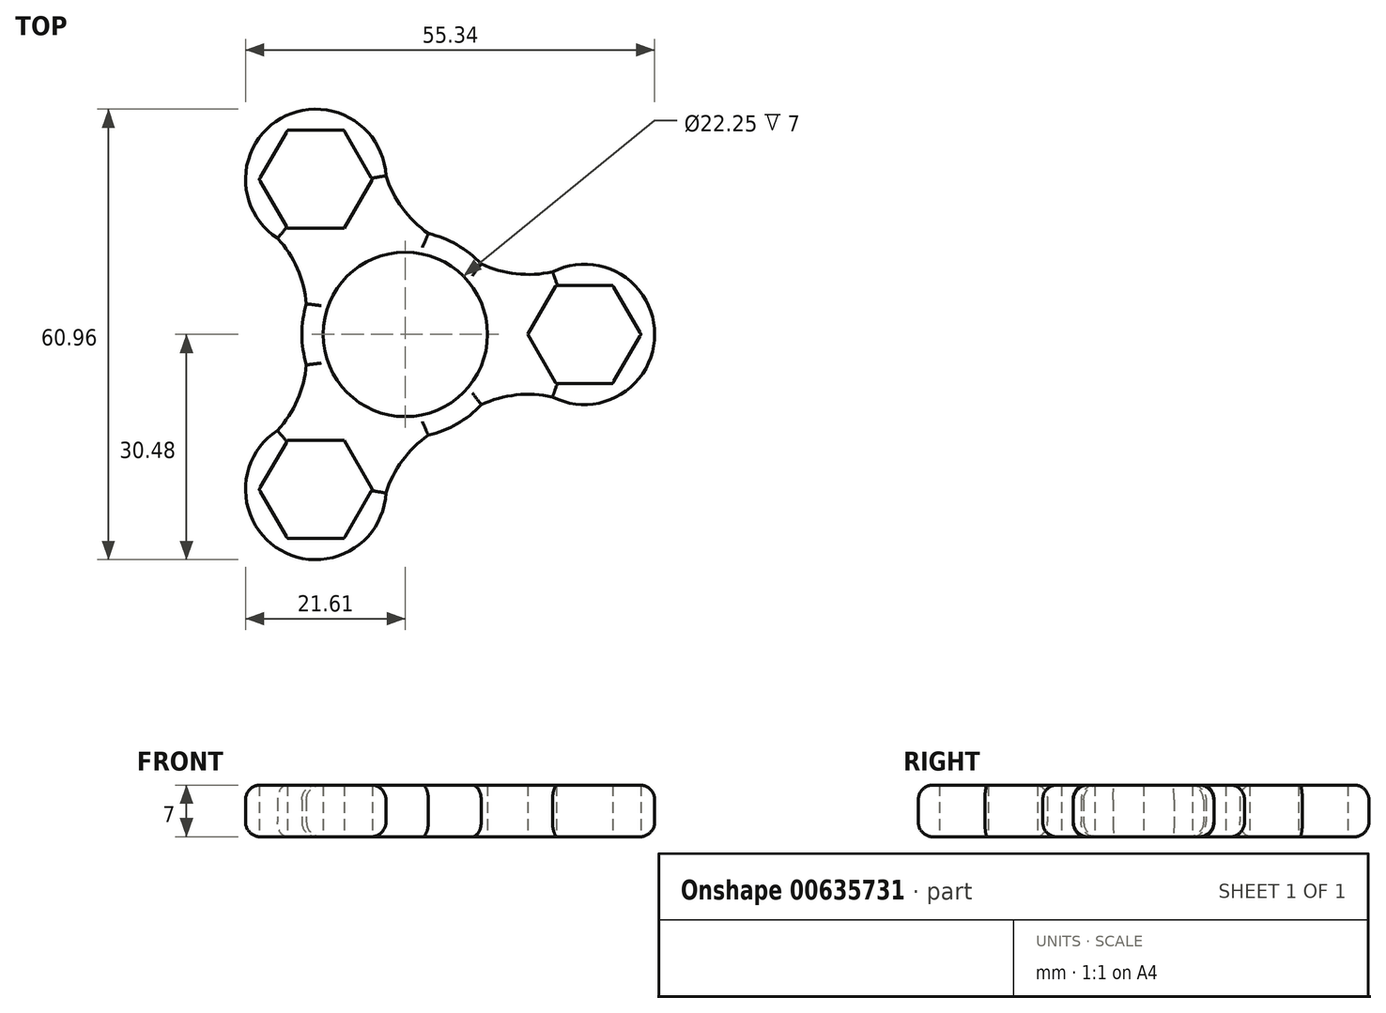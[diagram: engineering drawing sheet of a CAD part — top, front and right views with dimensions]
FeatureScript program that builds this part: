
annotation { "Feature Type Name" : "Feature", "Feature Type Description" : "" }
export const myFeature = defineFeature(function(context is Context, id is Id, definition is map)
    precondition{}
    {
        {
            var Q0;
            Q0=qCreatedBy(makeId("Top.planeOp"),FACE);
            var sketch = newSketch(context, id + "F0", { "sketchPlane" : qUnion([Q0])});
            skCircle(sketch, "E0", {"center": v(0, 0) * mm, "radius": 11.12 * mm});
            skLineSegment(sketch, "E1", {"start": v(0, 0) * mm, "end": v(30, 0) * mm, "construction": true});
            skCircle(sketch, "E2", {"center": v(24.23, 0) * mm, "radius": 9.5 * mm});
            skCircle(sketch, "E3", {"center": v(0, 0) * mm, "radius": 14 * mm});
            skArc(sketch, "E4", {"start": v(19.9, -8.46) * mm, "mid": v(15, -8.2) * mm, "end": v(10.26, -9.52) * mm});
            skArc(sketch, "E5.MirrorCS", {"start": v(19.9, 8.46) * mm, "mid": v(15, 8.2) * mm, "end": v(10.26, 9.52) * mm});
            skCircle(sketch, "E6.cCircle", {"center": v(24.23, 0) * mm, "radius": 6.62 * mm, "construction": true});
            skLineSegment(sketch, "E6.0", {"start": v(20.4, 6.62) * mm, "end": v(28.05, 6.62) * mm});
            skLineSegment(sketch, "E6.1", {"start": v(28.05, 6.62) * mm, "end": v(31.88, 0) * mm});
            skLineSegment(sketch, "E6.2", {"start": v(31.88, 0) * mm, "end": v(28.05, -6.62) * mm});
            skLineSegment(sketch, "E6.3", {"start": v(28.05, -6.62) * mm, "end": v(20.4, -6.63) * mm});
            skLineSegment(sketch, "E6.4", {"start": v(20.4, -6.63) * mm, "end": v(16.58, 0) * mm});
            skLineSegment(sketch, "E6.5", {"start": v(16.58, 0) * mm, "end": v(20.4, 6.63) * mm});
            skPoint(sketch, "E6.0.midPoint", {"position": v(24.23, 6.62) * mm});
            skLineSegment(sketch, "E7.1.0", {"start": v(-15.94, 14.36) * mm, "end": v(-19.76, 20.98) * mm});
            skArc(sketch, "E7.1.1", {"start": v(-2.63, 21.47) * mm, "mid": v(-0.4, 17.09) * mm, "end": v(3.12, 13.65) * mm});
            skLineSegment(sketch, "E7.1.2", {"start": v(-15.94, 27.6) * mm, "end": v(-8.29, 27.6) * mm});
            skArc(sketch, "E7.1.3", {"start": v(-17.28, 13.01) * mm, "mid": v(-14.6, 8.9) * mm, "end": v(-13.38, 4.12) * mm});
            skCircle(sketch, "E7.1.4", {"center": v(-12.11, 20.98) * mm, "radius": 6.62 * mm, "construction": true});
            skLineSegment(sketch, "E7.1.5", {"start": v(0, 0) * mm, "end": v(-15, 25.98) * mm, "construction": true});
            skCircle(sketch, "E7.1.6", {"center": v(-12.11, 20.98) * mm, "radius": 9.5 * mm});
            skLineSegment(sketch, "E7.1.7", {"start": v(-19.76, 20.98) * mm, "end": v(-15.94, 27.6) * mm});
            skLineSegment(sketch, "E7.1.8", {"start": v(-8.29, 27.6) * mm, "end": v(-4.46, 20.98) * mm});
            skLineSegment(sketch, "E7.1.9", {"start": v(-4.46, 20.98) * mm, "end": v(-8.29, 14.36) * mm});
            skLineSegment(sketch, "E7.1.10", {"start": v(-8.29, 14.36) * mm, "end": v(-15.94, 14.36) * mm});
            skPoint(sketch, "E7.1.11", {"position": v(-17.85, 17.67) * mm});
            skLineSegment(sketch, "E7.2.0", {"start": v(-4.46, -20.98) * mm, "end": v(-8.29, -27.6) * mm});
            skArc(sketch, "E7.2.1", {"start": v(-17.28, -13.01) * mm, "mid": v(-14.6, -8.9) * mm, "end": v(-13.38, -4.12) * mm});
            skLineSegment(sketch, "E7.2.2", {"start": v(-15.94, -27.6) * mm, "end": v(-19.76, -20.98) * mm});
            skArc(sketch, "E7.2.3", {"start": v(-2.63, -21.47) * mm, "mid": v(-0.4, -17.09) * mm, "end": v(3.12, -13.65) * mm});
            skCircle(sketch, "E7.2.4", {"center": v(-12.11, -20.98) * mm, "radius": 6.62 * mm, "construction": true});
            skLineSegment(sketch, "E7.2.5", {"start": v(0, 0) * mm, "end": v(-15, -25.98) * mm, "construction": true});
            skCircle(sketch, "E7.2.6", {"center": v(-12.11, -20.98) * mm, "radius": 9.5 * mm});
            skLineSegment(sketch, "E7.2.7", {"start": v(-8.29, -27.6) * mm, "end": v(-15.94, -27.6) * mm});
            skLineSegment(sketch, "E7.2.8", {"start": v(-19.76, -20.98) * mm, "end": v(-15.94, -14.36) * mm});
            skLineSegment(sketch, "E7.2.9", {"start": v(-15.94, -14.36) * mm, "end": v(-8.29, -14.36) * mm});
            skLineSegment(sketch, "E7.2.10", {"start": v(-8.29, -14.36) * mm, "end": v(-4.46, -20.98) * mm});
            skPoint(sketch, "E7.2.11", {"position": v(-6.38, -24.3) * mm});
            skSolve(sketch);
        }
        {
            var Q0;
            Q0=makeQuery(id+"F0.imprint","IMPRINT",FACE,{"disambiguationData":[TD([[makeQuery(id+"F0.imprint","IMPRINT",EDGE,{"derivedFrom":sQuery(id+"F0.wireOp",EDGE,"0df89d4a-0bd4-4ad1-abb0-4ab84ff28107.1.3")}),-1.0]])]});
            var Q1;
            {var subQ0=sQuery(id+"F0.wireOp",EDGE,"0df89d4a-0bd4-4ad1-abb0-4ab84ff28107.1.0");Q1=makeQuery(id+"F0.imprint","IMPRINT",FACE,{"disambiguationData":[TD([[makeQuery(id+"F0.imprint","IMPRINT",EDGE,{"derivedFrom":subQ0}),1.0]])]});}
            var Q2;
            Q2=makeQuery(id+"F0.imprint","IMPRINT",FACE,{"disambiguationData":[TD([[makeQuery(id+"F0.imprint","IMPRINT",EDGE,{"derivedFrom":sQuery(id+"F0.wireOp",EDGE,"E0")}),-1.0]])]});
            var Q3;
            {var subQ0=sQuery(id+"F0.wireOp",EDGE,"E4");Q3=makeQuery(id+"F0.imprint","IMPRINT",FACE,{"disambiguationData":[TD([[makeQuery(id+"F0.imprint","IMPRINT",EDGE,{"derivedFrom":subQ0}),-1.0]])]});}
            var Q4;
            Q4=makeQuery(id+"F0.imprint","IMPRINT",FACE,{"disambiguationData":[TD([[makeQuery(id+"F0.imprint","IMPRINT",EDGE,{"derivedFrom":sQuery(id+"F0.wireOp",EDGE,"yqVcjg71-0tow-opGA-WTYz-QMPVO2lDSPor")}),-1.0]])]});
            var Q5;
            {var subQ0=sQuery(id+"F0.wireOp",EDGE,"0df89d4a-0bd4-4ad1-abb0-4ab84ff28107.2.0");Q5=makeQuery(id+"F0.imprint","IMPRINT",FACE,{"disambiguationData":[TD([[makeQuery(id+"F0.imprint","IMPRINT",EDGE,{"derivedFrom":subQ0}),1.0]])]});}
            var Q6;
            Q6=makeQuery(id+"F0.imprint","IMPRINT",FACE,{"disambiguationData":[TD([[makeQuery(id+"F0.imprint","IMPRINT",EDGE,{"derivedFrom":sQuery(id+"F0.wireOp",EDGE,"0df89d4a-0bd4-4ad1-abb0-4ab84ff28107.2.3")}),-1.0]])]});
            var Q7;
            Q7=makeQuery(id+"F0.imprint","IMPRINT",FACE,{"disambiguationData":[TD([[makeQuery(id+"F0.imprint","IMPRINT",EDGE,{"derivedFrom":sQuery(id+"F0.wireOp",EDGE,"d223a131-a13d-45e3-9094-9db3f5cdf163.0")}),1.0]])]});
            var Q8;
            Q8=makeQuery(id+"F0.imprint","IMPRINT",FACE,{"disambiguationData":[TD([[makeQuery(id+"F0.imprint","IMPRINT",EDGE,{"derivedFrom":sQuery(id+"F0.wireOp",EDGE,"E6.0")}),1.0]])]});
            var Q9;
            Q9=makeQuery(id+"F0.imprint","IMPRINT",FACE,{"disambiguationData":[TD([[makeQuery(id+"F0.imprint","IMPRINT",EDGE,{"derivedFrom":sQuery(id+"F0.wireOp",EDGE,"9b35a66b-6c7d-4a83-b0f2-d91667951e34.0")}),1.0]])]});
            var Q10;
            {var subQ0=sQuery(id+"F0.wireOp",EDGE,"E7.1.1");Q10=makeQuery(id+"F0.imprint","IMPRINT",FACE,{"disambiguationData":[TD([[makeQuery(id+"F0.imprint","IMPRINT",EDGE,{"derivedFrom":subQ0}),-1.0]])]});}
            var Q11;
            Q11=makeQuery(id+"F0.imprint","IMPRINT",FACE,{"disambiguationData":[TD([[makeQuery(id+"F0.imprint","IMPRINT",EDGE,{"derivedFrom":sQuery(id+"F0.wireOp",EDGE,"E7.1.0")}),1.0]])]});
            var Q12;
            {var subQ0=sQuery(id+"F0.wireOp",EDGE,"E7.2.1");Q12=makeQuery(id+"F0.imprint","IMPRINT",FACE,{"disambiguationData":[TD([[makeQuery(id+"F0.imprint","IMPRINT",EDGE,{"derivedFrom":subQ0}),-1.0]])]});}
            var Q13;
            Q13=makeQuery(id+"F0.imprint","IMPRINT",FACE,{"disambiguationData":[TD([[makeQuery(id+"F0.imprint","IMPRINT",EDGE,{"derivedFrom":sQuery(id+"F0.wireOp",EDGE,"E7.2.0")}),1.0]])]});
            extrude(context, id + "F1", {"entities" : qUnion([Q0, Q1, Q2, Q3, Q4, Q5, Q6, Q7, Q8, Q9, Q10, Q11, Q12, Q13]), "depth" : 7 * mm, "offsetDistance" : 25 * mm});
        }
        {
            var Q0;
            Q0=makeQuery(id+"F1.opExtrude","CAP_EDGE",EDGE,{"disambiguationData":[OSD([sQuery(id+"F0.wireOp",EDGE,"E7.1.6")])],"isStart":false});
            var Q1;
            Q1=makeQuery(id+"F1.opExtrude","CAP_EDGE",EDGE,{"disambiguationData":[OSD([sQuery(id+"F0.wireOp",EDGE,"E7.1.3")])],"isStart":false});
            var Q2;
            {var subQ0=sQuery(id+"F0.wireOp",EDGE,"E3");Q2=makeQuery(id+"F1.opExtrude","CAP_EDGE",EDGE,{"disambiguationData":[OSD([subQ0]),TDD([makeQuery(id+"F0.imprint","IMPRINT",EDGE,{"disambiguationData":[TD([[makeQuery(id+"F0.imprint","INTERSECT",VERTEX,{"derivedFrom":[subQ0,sQuery(id+"F0.wireOp",EDGE,"E7.1.3")]}),-1.0]])],"derivedFrom":subQ0})])],"isStart":false});}
            var Q3;
            Q3=makeQuery(id+"F1.opExtrude","CAP_EDGE",EDGE,{"disambiguationData":[OSD([sQuery(id+"F0.wireOp",EDGE,"E7.2.1")])],"isStart":false});
            var Q4;
            Q4=makeQuery(id+"F1.opExtrude","CAP_EDGE",EDGE,{"disambiguationData":[OSD([sQuery(id+"F0.wireOp",EDGE,"E7.2.6")])],"isStart":false});
            var Q5;
            Q5=makeQuery(id+"F1.opExtrude","CAP_EDGE",EDGE,{"disambiguationData":[OSD([sQuery(id+"F0.wireOp",EDGE,"E7.2.3")])],"isStart":false});
            var Q6;
            {var subQ0=sQuery(id+"F0.wireOp",EDGE,"E3");Q6=makeQuery(id+"F1.opExtrude","CAP_EDGE",EDGE,{"disambiguationData":[OSD([subQ0]),TDD([makeQuery(id+"F0.imprint","IMPRINT",EDGE,{"disambiguationData":[TD([[makeQuery(id+"F0.imprint","INTERSECT",VERTEX,{"derivedFrom":[subQ0,sQuery(id+"F0.wireOp",EDGE,"E4")]}),1.0]])],"derivedFrom":subQ0})])],"isStart":false});}
            var Q7;
            Q7=makeQuery(id+"F1.opExtrude","CAP_EDGE",EDGE,{"disambiguationData":[OSD([sQuery(id+"F0.wireOp",EDGE,"E4")])],"isStart":false});
            var Q8;
            Q8=makeQuery(id+"F1.opExtrude","CAP_EDGE",EDGE,{"disambiguationData":[OSD([sQuery(id+"F0.wireOp",EDGE,"E2")])],"isStart":false});
            var Q9;
            Q9=makeQuery(id+"F1.opExtrude","CAP_EDGE",EDGE,{"disambiguationData":[OSD([sQuery(id+"F0.wireOp",EDGE,"E5.MirrorCS")])],"isStart":false});
            var Q10;
            {var subQ0=sQuery(id+"F0.wireOp",EDGE,"E3");Q10=makeQuery(id+"F1.opExtrude","CAP_EDGE",EDGE,{"disambiguationData":[OSD([subQ0]),TDD([makeQuery(id+"F0.imprint","IMPRINT",EDGE,{"disambiguationData":[TD([[makeQuery(id+"F0.imprint","INTERSECT",VERTEX,{"derivedFrom":[subQ0,sQuery(id+"F0.wireOp",EDGE,"E5.MirrorCS")]}),-1.0]])],"derivedFrom":subQ0})])],"isStart":false});}
            var Q11;
            Q11=makeQuery(id+"F1.opExtrude","CAP_EDGE",EDGE,{"disambiguationData":[OSD([sQuery(id+"F0.wireOp",EDGE,"E7.1.1")])],"isStart":false});
            var Q12;
            Q12=makeQuery(id+"F1.opExtrude","CAP_EDGE",EDGE,{"disambiguationData":[OSD([sQuery(id+"F0.wireOp",EDGE,"E7.2.6")])],"isStart":true});
            var Q13;
            Q13=makeQuery(id+"F1.opExtrude","CAP_EDGE",EDGE,{"disambiguationData":[OSD([sQuery(id+"F0.wireOp",EDGE,"E7.2.1")])],"isStart":true});
            var Q14;
            {var subQ0=sQuery(id+"F0.wireOp",EDGE,"E3");Q14=makeQuery(id+"F1.opExtrude","CAP_EDGE",EDGE,{"disambiguationData":[OSD([subQ0]),TDD([makeQuery(id+"F0.imprint","IMPRINT",EDGE,{"disambiguationData":[TD([[makeQuery(id+"F0.imprint","INTERSECT",VERTEX,{"derivedFrom":[subQ0,sQuery(id+"F0.wireOp",EDGE,"E7.1.3")]}),-1.0]])],"derivedFrom":subQ0})])],"isStart":true});}
            var Q15;
            Q15=makeQuery(id+"F1.opExtrude","CAP_EDGE",EDGE,{"disambiguationData":[OSD([sQuery(id+"F0.wireOp",EDGE,"E7.1.3")])],"isStart":true});
            var Q16;
            Q16=makeQuery(id+"F1.opExtrude","CAP_EDGE",EDGE,{"disambiguationData":[OSD([sQuery(id+"F0.wireOp",EDGE,"E7.1.6")])],"isStart":true});
            var Q17;
            Q17=makeQuery(id+"F1.opExtrude","CAP_EDGE",EDGE,{"disambiguationData":[OSD([sQuery(id+"F0.wireOp",EDGE,"E7.1.1")])],"isStart":true});
            var Q18;
            {var subQ0=sQuery(id+"F0.wireOp",EDGE,"E3");Q18=makeQuery(id+"F1.opExtrude","CAP_EDGE",EDGE,{"disambiguationData":[OSD([subQ0]),TDD([makeQuery(id+"F0.imprint","IMPRINT",EDGE,{"disambiguationData":[TD([[makeQuery(id+"F0.imprint","INTERSECT",VERTEX,{"derivedFrom":[subQ0,sQuery(id+"F0.wireOp",EDGE,"E5.MirrorCS")]}),-1.0]])],"derivedFrom":subQ0})])],"isStart":true});}
            var Q19;
            Q19=makeQuery(id+"F1.opExtrude","CAP_EDGE",EDGE,{"disambiguationData":[OSD([sQuery(id+"F0.wireOp",EDGE,"E5.MirrorCS")])],"isStart":true});
            var Q20;
            Q20=makeQuery(id+"F1.opExtrude","CAP_EDGE",EDGE,{"disambiguationData":[OSD([sQuery(id+"F0.wireOp",EDGE,"E2")])],"isStart":true});
            var Q21;
            Q21=makeQuery(id+"F1.opExtrude","CAP_EDGE",EDGE,{"disambiguationData":[OSD([sQuery(id+"F0.wireOp",EDGE,"E4")])],"isStart":true});
            var Q22;
            {var subQ0=sQuery(id+"F0.wireOp",EDGE,"E3");Q22=makeQuery(id+"F1.opExtrude","CAP_EDGE",EDGE,{"disambiguationData":[OSD([subQ0]),TDD([makeQuery(id+"F0.imprint","IMPRINT",EDGE,{"disambiguationData":[TD([[makeQuery(id+"F0.imprint","INTERSECT",VERTEX,{"derivedFrom":[subQ0,sQuery(id+"F0.wireOp",EDGE,"E4")]}),1.0]])],"derivedFrom":subQ0})])],"isStart":true});}
            var Q23;
            Q23=makeQuery(id+"F1.opExtrude","CAP_EDGE",EDGE,{"disambiguationData":[OSD([sQuery(id+"F0.wireOp",EDGE,"E7.2.3")])],"isStart":true});
            fillet(context, id + "F2", {"entities" : qUnion([Q0, Q1, Q2, Q3, Q4, Q5, Q6, Q7, Q8, Q9, Q10, Q11, Q12, Q13, Q14, Q15, Q16, Q17, Q18, Q19, Q20, Q21, Q22, Q23]), "radius" : 2 * mm, "tangentPropagation" : true, "allowEdgeOverflow" : false});
        }
    });
